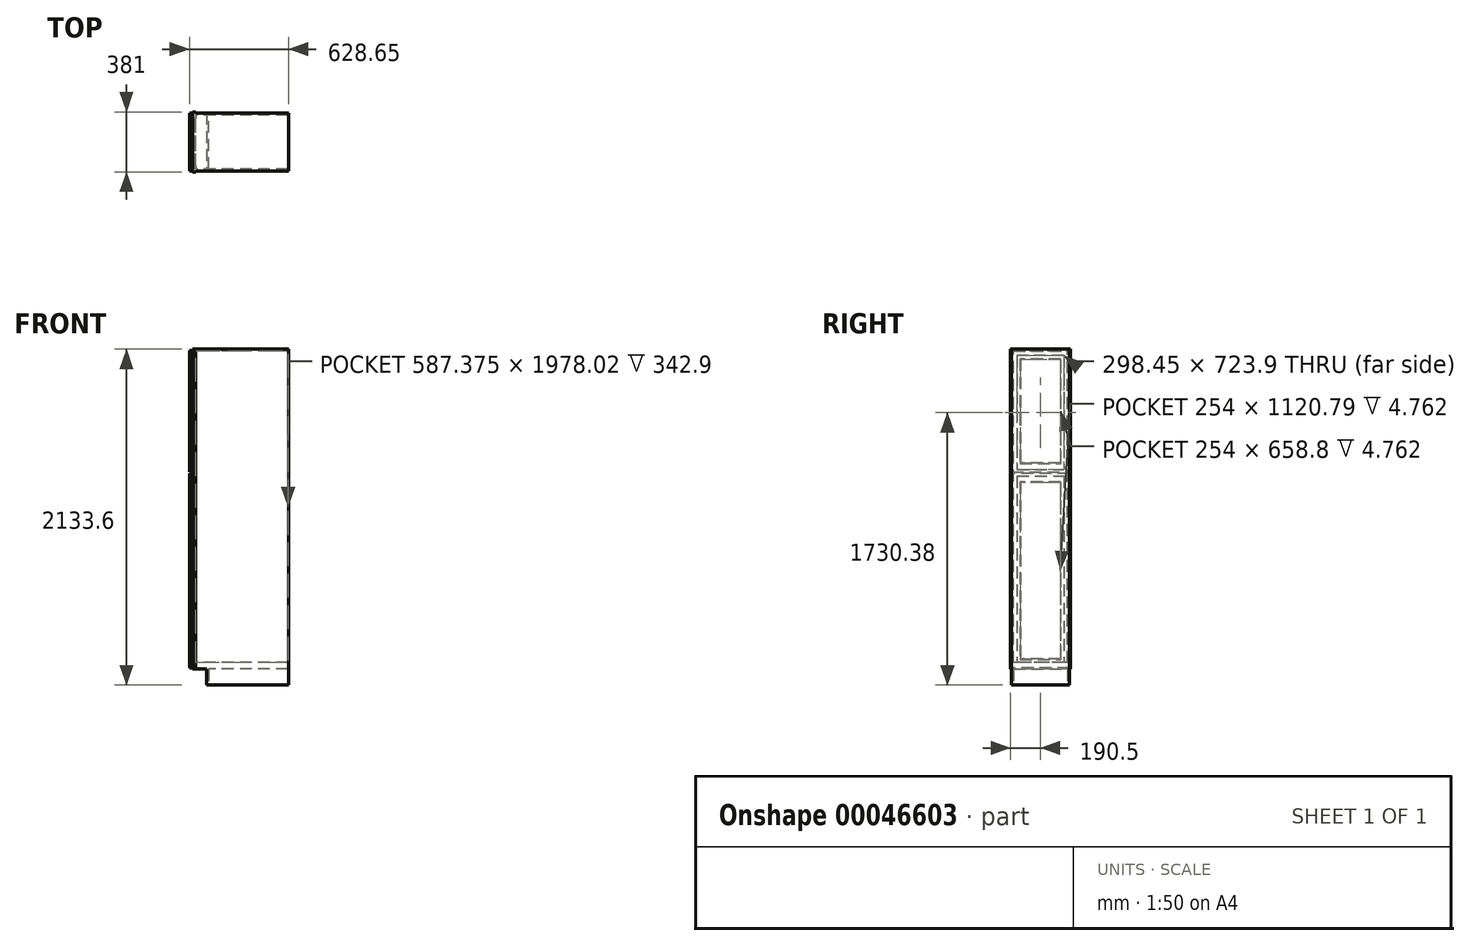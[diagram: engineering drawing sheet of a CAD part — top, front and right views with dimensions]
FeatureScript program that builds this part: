
annotation { "Feature Type Name" : "Feature", "Feature Type Description" : "" }
export const myFeature = defineFeature(function(context is Context, id is Id, definition is map)
    precondition{}
    {
        {
            var Q0;
            Q0=qCreatedBy(makeId("Front.planeOp"),FACE);
            var sketch = newSketch(context, id + "F0", { "sketchPlane" : qUnion([Q0])});
            skLineSegment(sketch, "E0.bottom", {"start": v(-304.8, -1066.8) * mm, "end": v(304.8, -1066.8) * mm});
            skLineSegment(sketch, "E0.top", {"start": v(-304.8, 1066.8) * mm, "end": v(304.8, 1066.8) * mm});
            skLineSegment(sketch, "E0.left", {"start": v(-304.8, -1066.8) * mm, "end": v(-304.8, 1066.8) * mm});
            skLineSegment(sketch, "E0.right", {"start": v(304.8, -1066.8) * mm, "end": v(304.8, 1066.8) * mm});
            skLineSegment(sketch, "E1", {"start": v(-304.8, -1066.8) * mm, "end": v(304.8, 1066.8) * mm, "construction": true});
            skSolve(sketch);
        }
        {
            var Q0;
            Q0=qSketchRegion(id+"F0",true);
            extrude(context, id + "F1", {"entities" : qUnion([Q0]), "oppositeDirection" : true, "depth" : 381 * mm});
        }
        {
            var Q0;
            Q0=makeQuery(id+"F1.opExtrude","CAP_FACE",FACE,{"disambiguationData":[OSD([sQuery(id+"F0.wireOp",EDGE,"E0.bottom"),sQuery(id+"F0.wireOp",EDGE,"E0.top"),sQuery(id+"F0.wireOp",EDGE,"E0.left"),sQuery(id+"F0.wireOp",EDGE,"E0.right")])],"isStart":true});
            var sketch = newSketch(context, id + "F2", { "sketchPlane" : qUnion([Q0])});
            skLineSegment(sketch, "E2.bottom", {"start": v(-304.8, -1066.8) * mm, "end": v(-215.9, -1066.8) * mm});
            skLineSegment(sketch, "E2.top", {"start": v(-304.8, -965.2) * mm, "end": v(-215.9, -965.2) * mm});
            skLineSegment(sketch, "E2.left", {"start": v(-304.8, -1066.8) * mm, "end": v(-304.8, -965.2) * mm});
            skLineSegment(sketch, "E2.right", {"start": v(-215.9, -1066.8) * mm, "end": v(-215.9, -965.2) * mm});
            skSolve(sketch);
        }
        {
            var Q0;
            Q0=qSketchRegion(id+"F2",true);
            extrude(context, id + "F3", {"entities" : qUnion([Q0]), "operationType" : NewBodyOperationType.REMOVE, "endBound" : BoundingType.THROUGH_ALL, "oppositeDirection" : true, "depth" : 25.4 * mm});
        }
        {
            var Q0;
            Q0=makeQuery(id+"F1.opExtrude","SWEPT_FACE",FACE,{"disambiguationData":[OSD([sQuery(id+"F0.wireOp",EDGE,"E0.left")])]});
            var sketch = newSketch(context, id + "F4", { "sketchPlane" : qUnion([Q0])});
            skLineSegment(sketch, "E3.bottom", {"start": v(-339.73, 1025.53) * mm, "end": v(-41.28, 1025.53) * mm});
            skLineSegment(sketch, "E3.top", {"start": v(-339.73, -923.93) * mm, "end": v(-41.27, -923.93) * mm});
            skLineSegment(sketch, "E3.left", {"start": v(-339.73, 1025.53) * mm, "end": v(-339.73, -923.93) * mm});
            skLineSegment(sketch, "E3.right", {"start": v(-41.28, 1025.53) * mm, "end": v(-41.27, -923.93) * mm});
            skSolve(sketch);
        }
        {
            var Q0;
            Q0=qSketchRegion(id+"F4",true);
            extrude(context, id + "F5", {"entities" : qUnion([Q0]), "operationType" : NewBodyOperationType.REMOVE, "oppositeDirection" : true, "depth" : 19.05 * mm});
        }
        {
            var Q0;
            Q0=makeQuery(id+"F1.opExtrude","SWEPT_FACE",FACE,{"disambiguationData":[OSD([sQuery(id+"F0.wireOp",EDGE,"E0.top")])]});
            var sketch = newSketch(context, id + "F6", { "sketchPlane" : qUnion([Q0])});
            skLineSegment(sketch, "E4.bottom", {"start": v(304.8, 381) * mm, "end": v(-285.75, 381) * mm});
            skLineSegment(sketch, "E4.top", {"start": v(304.8, 374.65) * mm, "end": v(-285.75, 374.65) * mm});
            skLineSegment(sketch, "E4.left", {"start": v(304.8, 381) * mm, "end": v(304.8, 374.65) * mm});
            skLineSegment(sketch, "E4.right", {"start": v(-285.75, 381) * mm, "end": v(-285.75, 374.65) * mm});
            skLineSegment(sketch, "E5.bottom", {"start": v(304.8, 0) * mm, "end": v(-285.75, 0) * mm});
            skLineSegment(sketch, "E5.top", {"start": v(304.8, 6.35) * mm, "end": v(-285.75, 6.35) * mm});
            skLineSegment(sketch, "E5.left", {"start": v(304.8, 0) * mm, "end": v(304.8, 6.35) * mm});
            skLineSegment(sketch, "E5.right", {"start": v(-285.75, 0) * mm, "end": v(-285.75, 6.35) * mm});
            skSolve(sketch);
        }
        {
            var Q0;
            Q0=qSketchRegion(id+"F6",true);
            extrude(context, id + "F7", {"entities" : qUnion([Q0]), "operationType" : NewBodyOperationType.REMOVE, "endBound" : BoundingType.THROUGH_ALL, "oppositeDirection" : true, "depth" : 25.4 * mm});
        }
        {
            var Q0;
            Q0=makeQuery(id+"F1.opExtrude","SWEPT_FACE",FACE,{"disambiguationData":[OSD([sQuery(id+"F0.wireOp",EDGE,"E0.top")])]});
            var sketch = newSketch(context, id + "F8", { "sketchPlane" : qUnion([Q0])});
            skLineSegment(sketch, "E6.bottom", {"start": v(301.63, 361.95) * mm, "end": v(-285.75, 361.95) * mm});
            skLineSegment(sketch, "E6.top", {"start": v(301.63, 19.05) * mm, "end": v(-285.75, 19.05) * mm});
            skLineSegment(sketch, "E6.left", {"start": v(301.63, 361.95) * mm, "end": v(301.63, 19.05) * mm});
            skLineSegment(sketch, "E6.right", {"start": v(-285.75, 361.95) * mm, "end": v(-285.75, 19.05) * mm});
            skSolve(sketch);
        }
        {
            var Q0;
            Q0=qSketchRegion(id+"F8",true);
            var Q1;
            Q1=makeQuery(id+"F5.boolean.opBoolean","COPY",FACE,{"derivedFrom":makeQuery(id+"F5.opExtrude","SWEPT_FACE",FACE,{"disambiguationData":[OSD([sQuery(id+"F4.wireOp",EDGE,"E3.top")])]})});
            extrude(context, id + "F9", {"entities" : qUnion([Q0]), "operationType" : NewBodyOperationType.REMOVE, "endBound" : BoundingType.UP_TO_SURFACE, "oppositeDirection" : true, "endBoundEntityFace" : qUnion([Q1]), "depth" : 25.4 * mm});
        }
        {
            var Q0;
            Q0=makeQuery(id+"F1.opExtrude","SWEPT_FACE",FACE,{"disambiguationData":[OSD([sQuery(id+"F0.wireOp",EDGE,"E0.left")])]});
            var sketch = newSketch(context, id + "F10", { "sketchPlane" : qUnion([Q0])});
            skLineSegment(sketch, "E7.bottom", {"start": v(-339.73, 301.63) * mm, "end": v(-41.28, 301.63) * mm});
            skLineSegment(sketch, "E7.top", {"start": v(-339.73, 260.35) * mm, "end": v(-41.28, 260.35) * mm});
            skLineSegment(sketch, "E7.left", {"start": v(-339.73, 301.63) * mm, "end": v(-339.73, 260.35) * mm});
            skLineSegment(sketch, "E7.right", {"start": v(-41.28, 301.63) * mm, "end": v(-41.28, 260.35) * mm});
            skSolve(sketch);
        }
        {
            var Q0;
            Q0=qSketchRegion(id+"F10",true);
            var Q1;
            Q1=makeQuery(id+"F9.boolean.opBoolean","COPY",FACE,{"derivedFrom":makeQuery(id+"F9.opExtrude","SWEPT_FACE",FACE,{"disambiguationData":[OSD([sQuery(id+"F8.wireOp",EDGE,"E6.right")])]})});
            extrude(context, id + "F11", {"entities" : qUnion([Q0]), "operationType" : NewBodyOperationType.ADD, "endBound" : BoundingType.UP_TO_SURFACE, "oppositeDirection" : true, "endBoundEntityFace" : qUnion([Q1]), "depth" : 25.4 * mm});
        }
        {
            var Q0;
            Q0=makeQuery(id+"F11.boolean.opBoolean","MERGE",FACE,{"derivedFrom":[makeQuery(id+"F1.opExtrude","SWEPT_FACE",FACE,{"disambiguationData":[OSD([sQuery(id+"F0.wireOp",EDGE,"E0.left")])]}),makeQuery(id+"F11.opExtrude","CAP_FACE",FACE,{"disambiguationData":[OSD([sQuery(id+"F10.wireOp",EDGE,"E7.bottom"),sQuery(id+"F10.wireOp",EDGE,"E7.top"),sQuery(id+"F10.wireOp",EDGE,"E7.left"),sQuery(id+"F10.wireOp",EDGE,"E7.right")])],"isStart":true})]});
            var sketch = newSketch(context, id + "F12", { "sketchPlane" : qUnion([Q0])});
            skLineSegment(sketch, "E8.bottom", {"start": v(-374.65, 277.83) * mm, "end": v(-6.35, 277.83) * mm});
            skLineSegment(sketch, "E8.top", {"start": v(-374.65, -957.26) * mm, "end": v(-6.35, -957.26) * mm});
            skLineSegment(sketch, "E8.left", {"start": v(-374.65, 277.83) * mm, "end": v(-374.65, -957.26) * mm});
            skLineSegment(sketch, "E8.right", {"start": v(-6.35, 277.83) * mm, "end": v(-6.35, -957.26) * mm});
            skLineSegment(sketch, "E9.bottom", {"start": v(-317.5, 220.68) * mm, "end": v(-63.5, 220.68) * mm});
            skLineSegment(sketch, "E9.top", {"start": v(-317.5, -900.11) * mm, "end": v(-63.5, -900.11) * mm});
            skLineSegment(sketch, "E9.left", {"start": v(-317.5, 220.68) * mm, "end": v(-317.5, -900.11) * mm});
            skLineSegment(sketch, "E9.right", {"start": v(-63.5, 220.68) * mm, "end": v(-63.5, -900.11) * mm});
            skLineSegment(sketch, "E10", {"start": v(-6.35, 260.35) * mm, "end": v(-6.35, -923.93) * mm, "construction": true});
            skLineSegment(sketch, "E11.bottom", {"start": v(-6.35, 1058.86) * mm, "end": v(-374.65, 1058.86) * mm});
            skLineSegment(sketch, "E11.top", {"start": v(-6.35, 285.76) * mm, "end": v(-374.65, 285.76) * mm});
            skLineSegment(sketch, "E11.left", {"start": v(-6.35, 1058.86) * mm, "end": v(-6.35, 285.76) * mm});
            skLineSegment(sketch, "E11.right", {"start": v(-374.65, 1058.86) * mm, "end": v(-374.65, 285.76) * mm});
            skLineSegment(sketch, "E12.bottom", {"start": v(-317.5, 1001.71) * mm, "end": v(-63.5, 1001.71) * mm});
            skLineSegment(sketch, "E12.top", {"start": v(-317.5, 342.91) * mm, "end": v(-63.5, 342.91) * mm});
            skLineSegment(sketch, "E12.left", {"start": v(-317.5, 1001.71) * mm, "end": v(-317.5, 342.91) * mm});
            skLineSegment(sketch, "E12.right", {"start": v(-63.5, 1001.71) * mm, "end": v(-63.5, 342.91) * mm});
            skSolve(sketch);
        }
        {
            var Q0;
            Q0=qSketchRegion(id+"F12",true);
            extrude(context, id + "F13", {"entities" : qUnion([Q0]), "depth" : 19.05 * mm});
        }
        {
            var Q0;
            Q0=makeQuery(id+"F13.opExtrude","SWEPT_FACE",FACE,{"disambiguationData":[OSD([sQuery(id+"F12.wireOp",EDGE,"E9.top")])]});
            var sketch = newSketch(context, id + "F14", { "sketchPlane" : qUnion([Q0])});
            skLineSegment(sketch, "E13.bottom", {"start": v(-315.91, 317.5) * mm, "end": v(-309.56, 317.5) * mm});
            skLineSegment(sketch, "E13.top", {"start": v(-315.91, 63.5) * mm, "end": v(-309.56, 63.5) * mm});
            skLineSegment(sketch, "E13.left", {"start": v(-315.91, 317.5) * mm, "end": v(-315.91, 63.5) * mm});
            skLineSegment(sketch, "E13.right", {"start": v(-309.56, 317.5) * mm, "end": v(-309.56, 63.5) * mm});
            skSolve(sketch);
        }
        {
            var Q0;
            Q0=qSketchRegion(id+"F14",true);
            extrude(context, id + "F15", {"entities" : qUnion([Q0]), "operationType" : NewBodyOperationType.ADD, "endBound" : BoundingType.UP_TO_NEXT, "depth" : 25.4 * mm});
        }
        {
            var Q0;
            Q0=makeQuery(id+"F13.opExtrude","SWEPT_FACE",FACE,{"disambiguationData":[OSD([sQuery(id+"F12.wireOp",EDGE,"E12.top")])]});
            var sketch = newSketch(context, id + "F16", { "sketchPlane" : qUnion([Q0])});
            skLineSegment(sketch, "E14.bottom", {"start": v(-309.56, 317.5) * mm, "end": v(-315.91, 317.5) * mm});
            skLineSegment(sketch, "E14.top", {"start": v(-309.56, 63.5) * mm, "end": v(-315.91, 63.5) * mm});
            skLineSegment(sketch, "E14.left", {"start": v(-309.56, 317.5) * mm, "end": v(-309.56, 63.5) * mm});
            skLineSegment(sketch, "E14.right", {"start": v(-315.91, 317.5) * mm, "end": v(-315.91, 63.5) * mm});
            skSolve(sketch);
        }
        {
            var Q0;
            Q0=qSketchRegion(id+"F16",true);
            extrude(context, id + "F17", {"entities" : qUnion([Q0]), "operationType" : NewBodyOperationType.ADD, "endBound" : BoundingType.UP_TO_NEXT, "depth" : 25.4 * mm});
        }
        {
            var Q0;
            Q0=makeQuery(id+"F13.opExtrude","CAP_EDGE",EDGE,{"disambiguationData":[OSD([sQuery(id+"F12.wireOp",EDGE,"E9.left")])],"isStart":false});
            var Q1;
            Q1=makeQuery(id+"F13.opExtrude","CAP_EDGE",EDGE,{"disambiguationData":[OSD([sQuery(id+"F12.wireOp",EDGE,"E9.top")])],"isStart":false});
            var Q2;
            Q2=makeQuery(id+"F13.opExtrude","CAP_EDGE",EDGE,{"disambiguationData":[OSD([sQuery(id+"F12.wireOp",EDGE,"E9.right")])],"isStart":false});
            var Q3;
            Q3=makeQuery(id+"F13.opExtrude","CAP_EDGE",EDGE,{"disambiguationData":[OSD([sQuery(id+"F12.wireOp",EDGE,"E9.bottom")])],"isStart":false});
            var Q4;
            Q4=makeQuery(id+"F13.opExtrude","CAP_EDGE",EDGE,{"disambiguationData":[OSD([sQuery(id+"F12.wireOp",EDGE,"E12.top")])],"isStart":false});
            var Q5;
            Q5=makeQuery(id+"F13.opExtrude","CAP_EDGE",EDGE,{"disambiguationData":[OSD([sQuery(id+"F12.wireOp",EDGE,"E12.left")])],"isStart":false});
            var Q6;
            Q6=makeQuery(id+"F13.opExtrude","CAP_EDGE",EDGE,{"disambiguationData":[OSD([sQuery(id+"F12.wireOp",EDGE,"E12.right")])],"isStart":false});
            var Q7;
            Q7=makeQuery(id+"F13.opExtrude","CAP_EDGE",EDGE,{"disambiguationData":[OSD([sQuery(id+"F12.wireOp",EDGE,"E12.bottom")])],"isStart":false});
            chamfer(context, id + "F18", {"entities" : qUnion([Q0, Q1, Q2, Q3, Q4, Q5, Q6, Q7]), "width" : 3.17 * mm, "tangentPropagation" : true});
        }
        {
            var Q0;
            Q0=makeQuery(id+"F1.opExtrude","SWEPT_FACE",FACE,{"disambiguationData":[OSD([sQuery(id+"F0.wireOp",EDGE,"E0.bottom")])]});
            var sketch = newSketch(context, id + "F19", { "sketchPlane" : qUnion([Q0])});
            skLineSegment(sketch, "E15.bottom", {"start": v(301.63, -19.05) * mm, "end": v(-203.2, -19.05) * mm});
            skLineSegment(sketch, "E15.top", {"start": v(301.63, -361.95) * mm, "end": v(-203.2, -361.95) * mm});
            skLineSegment(sketch, "E15.left", {"start": v(301.63, -19.05) * mm, "end": v(301.63, -361.95) * mm});
            skLineSegment(sketch, "E15.right", {"start": v(-203.2, -19.05) * mm, "end": v(-203.2, -361.95) * mm});
            skSolve(sketch);
        }
        {
            var Q0;
            Q0=qSketchRegion(id+"F19",true);
            extrude(context, id + "F20", {"entities" : qUnion([Q0]), "operationType" : NewBodyOperationType.REMOVE, "oppositeDirection" : true, "depth" : 101.6 * mm});
        }
        {
            var Q0;
            Q0=makeQuery(id+"F11.boolean.opBoolean","MERGE",FACE,{"derivedFrom":[makeQuery(id+"F9.boolean.opBoolean","COPY",FACE,{"derivedFrom":makeQuery(id+"F9.opExtrude","SWEPT_FACE",FACE,{"disambiguationData":[OSD([sQuery(id+"F8.wireOp",EDGE,"E6.right")])]})}),makeQuery(id+"F11.opExtrude","CAP_FACE",FACE,{"disambiguationData":[OSD([sQuery(id+"F10.wireOp",EDGE,"E7.bottom"),sQuery(id+"F10.wireOp",EDGE,"E7.top"),sQuery(id+"F10.wireOp",EDGE,"E7.left"),sQuery(id+"F10.wireOp",EDGE,"E7.right")])],"isStart":false})]});
            var sketch = newSketch(context, id + "F21", { "sketchPlane" : qUnion([Q0])});
            skLineSegment(sketch, "E16.bottom", {"start": v(19.05, 1066.8) * mm, "end": v(361.95, 1066.8) * mm});
            skLineSegment(sketch, "E16.top", {"start": v(19.05, 1054.1) * mm, "end": v(361.95, 1054.1) * mm});
            skLineSegment(sketch, "E16.left", {"start": v(19.05, 1066.8) * mm, "end": v(19.05, 1054.1) * mm});
            skLineSegment(sketch, "E16.right", {"start": v(361.95, 1066.8) * mm, "end": v(361.95, 1054.1) * mm});
            skSolve(sketch);
        }
        {
            var Q0;
            Q0=makeQuery(id+"F21.imprint","IMPRINT",FACE,{"disambiguationData":[TD([[makeQuery(id+"F21.imprint","IMPRINT",EDGE,{"derivedFrom":sQuery(id+"F21.wireOp",EDGE,"E16.bottom")}),1.0]])]});
            extrude(context, id + "F22", {"entities" : qUnion([Q0]), "operationType" : NewBodyOperationType.ADD, "endBound" : BoundingType.UP_TO_NEXT, "depth" : 25.4 * mm});
        }
    });
